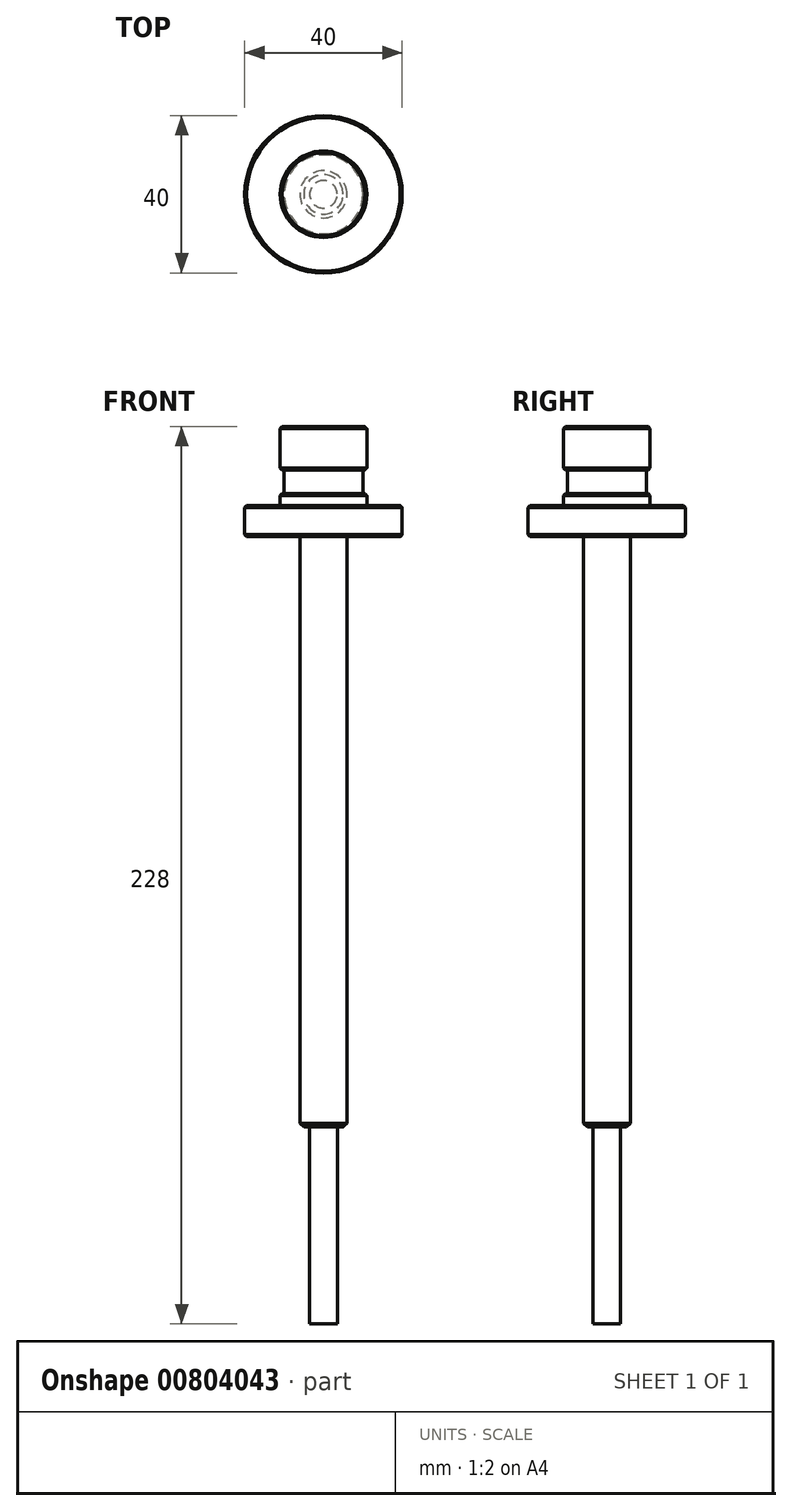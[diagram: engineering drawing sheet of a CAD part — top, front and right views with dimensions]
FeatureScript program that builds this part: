
annotation { "Feature Type Name" : "Feature", "Feature Type Description" : "" }
export const myFeature = defineFeature(function(context is Context, id is Id, definition is map)
    precondition{}
    {
        {
            var Q0;
            Q0=qCreatedBy(makeId("Top.planeOp"),FACE);
            var sketch = newSketch(context, id + "F0", { "sketchPlane" : qUnion([Q0])});
            skCircle(sketch, "E0", {"center": v(0, 0) * mm, "radius": 3.5 * mm});
            skSolve(sketch);
        }
        {
            var Q0;
            Q0 = qSketchRegion(id + "F0", true);
            extrude(context, id + "F1", {"entities" : qUnion([Q0]), "depth" : 50 * mm, "offsetDistance" : 25 * mm});
        }
        {
            var Q0;
            Q0=makeQuery(id+"F1.opExtrude","CAP_FACE",FACE,{"disambiguationData":[OSD([sQuery(id+"F0.wireOp",EDGE,"E0")])],"isStart":false});
            var sketch = newSketch(context, id + "F2", { "sketchPlane" : qUnion([Q0])});
            skCircle(sketch, "E1", {"center": v(0, 0) * mm, "radius": 6 * mm});
            skSolve(sketch);
        }
        {
            var Q0;
            Q0 = qSketchRegion(id + "F2", true);
            extrude(context, id + "F3", {"entities" : qUnion([Q0]), "operationType" : NewBodyOperationType.ADD, "depth" : 150 * mm, "offsetDistance" : 25 * mm});
        }
        {
            var Q0;
            Q0=makeQuery(id+"F3.opExtrude","CAP_FACE",FACE,{"disambiguationData":[OSD([sQuery(id+"F2.wireOp",EDGE,"E1")])],"isStart":false});
            var sketch = newSketch(context, id + "F4", { "sketchPlane" : qUnion([Q0])});
            skCircle(sketch, "E2", {"center": v(0, 0) * mm, "radius": 20 * mm});
            skSolve(sketch);
        }
        {
            var Q0;
            Q0 = qSketchRegion(id + "F4", true);
            extrude(context, id + "F5", {"entities" : qUnion([Q0]), "operationType" : NewBodyOperationType.ADD, "depth" : 7.9 * mm, "offsetDistance" : 25 * mm});
        }
        {
            var Q0;
            Q0=makeQuery(id+"F3.opExtrude","CAP_EDGE",EDGE,{"disambiguationData":[OSD([sQuery(id+"F2.wireOp",EDGE,"E1")])],"isStart":true});
            chamfer(context, id + "F6", {"entities" : qUnion([Q0]), "width" : 1 * mm, "tangentPropagation" : true});
        }
        {
            var Q0;
            Q0=makeQuery(id+"F5.opExtrude","CAP_EDGE",EDGE,{"disambiguationData":[OSD([sQuery(id+"F4.wireOp",EDGE,"E2")])],"isStart":true});
            var Q1;
            Q1=makeQuery(id+"F5.opExtrude","CAP_EDGE",EDGE,{"disambiguationData":[OSD([sQuery(id+"F4.wireOp",EDGE,"E2")])],"isStart":false});
            var Q2;
            Q2=makeQuery(id+"FwQAntjBeqZUWbU_1.opExtrude","CAP_EDGE",EDGE,{"disambiguationData":[OSD([sQuery(id+"FEITwo2KoTpGtd7_1.wireOp",EDGE,"Swwoo3wb-ijkb-Fegk-nYRY-PSU92WF0kA3k")])],"isStart":true});
            var Q3;
            Q3=makeQuery(id+"FwQAntjBeqZUWbU_1.opExtrude","CAP_EDGE",EDGE,{"disambiguationData":[OSD([sQuery(id+"FEITwo2KoTpGtd7_1.wireOp",EDGE,"Swwoo3wb-ijkb-Fegk-nYRY-PSU92WF0kA3k")])],"isStart":false});
            chamfer(context, id + "F7", {"entities" : qUnion([Q0, Q1, Q2, Q3]), "width" : .5 * mm, "tangentPropagation" : true});
        }
        {
            var Q0;
            Q0=makeQuery(id+"F5.opExtrude","CAP_FACE",FACE,{"disambiguationData":[OSD([sQuery(id+"F4.wireOp",EDGE,"E2")])],"isStart":false});
            var sketch = newSketch(context, id + "F8", { "sketchPlane" : qUnion([Q0])});
            skCircle(sketch, "E3", {"center": v(0, 0) * mm, "radius": 11 * mm});
            skSolve(sketch);
        }
        {
            var Q0;
            Q0 = qSketchRegion(id + "F8", true);
            extrude(context, id + "F9", {"entities" : qUnion([Q0]), "operationType" : NewBodyOperationType.ADD, "depth" : 3.1 * mm, "offsetDistance" : 25 * mm});
        }
        {
            var Q0;
            Q0=makeQuery(id+"F9.opExtrude","CAP_FACE",FACE,{"disambiguationData":[OSD([sQuery(id+"F8.wireOp",EDGE,"E3")])],"isStart":false});
            var sketch = newSketch(context, id + "F10", { "sketchPlane" : qUnion([Q0])});
            skCircle(sketch, "E4", {"center": v(0, 0) * mm, "radius": 10 * mm});
            skSolve(sketch);
        }
        {
            var Q0;
            Q0 = qSketchRegion(id + "F10", true);
            extrude(context, id + "F11", {"entities" : qUnion([Q0]), "operationType" : NewBodyOperationType.ADD, "depth" : 6 * mm, "offsetDistance" : 25 * mm});
        }
        {
            var Q0;
            Q0=makeQuery(id+"F11.opExtrude","CAP_FACE",FACE,{"disambiguationData":[OSD([sQuery(id+"F10.wireOp",EDGE,"E4")])],"isStart":false});
            var sketch = newSketch(context, id + "F12", { "sketchPlane" : qUnion([Q0])});
            skCircle(sketch, "E5", {"center": v(0, 0) * mm, "radius": 11 * mm});
            skSolve(sketch);
        }
        {
            var Q0;
            Q0 = qSketchRegion(id + "F12", true);
            extrude(context, id + "F13", {"entities" : qUnion([Q0]), "operationType" : NewBodyOperationType.ADD, "depth" : 11 * mm, "offsetDistance" : 25 * mm});
        }
        {
            var Q0;
            Q0=makeQuery(id+"F9.opExtrude","CAP_EDGE",EDGE,{"disambiguationData":[OSD([sQuery(id+"F8.wireOp",EDGE,"E3")])],"isStart":false});
            var Q1;
            Q1=makeQuery(id+"F13.opExtrude","CAP_EDGE",EDGE,{"disambiguationData":[OSD([sQuery(id+"F12.wireOp",EDGE,"E5")])],"isStart":true});
            var Q2;
            Q2=makeQuery(id+"F13.opExtrude","CAP_EDGE",EDGE,{"disambiguationData":[OSD([sQuery(id+"F12.wireOp",EDGE,"E5")])],"isStart":false});
            chamfer(context, id + "F14", {"entities" : qUnion([Q0, Q1, Q2]), "width" : .5 * mm, "tangentPropagation" : true});
        }
    });
